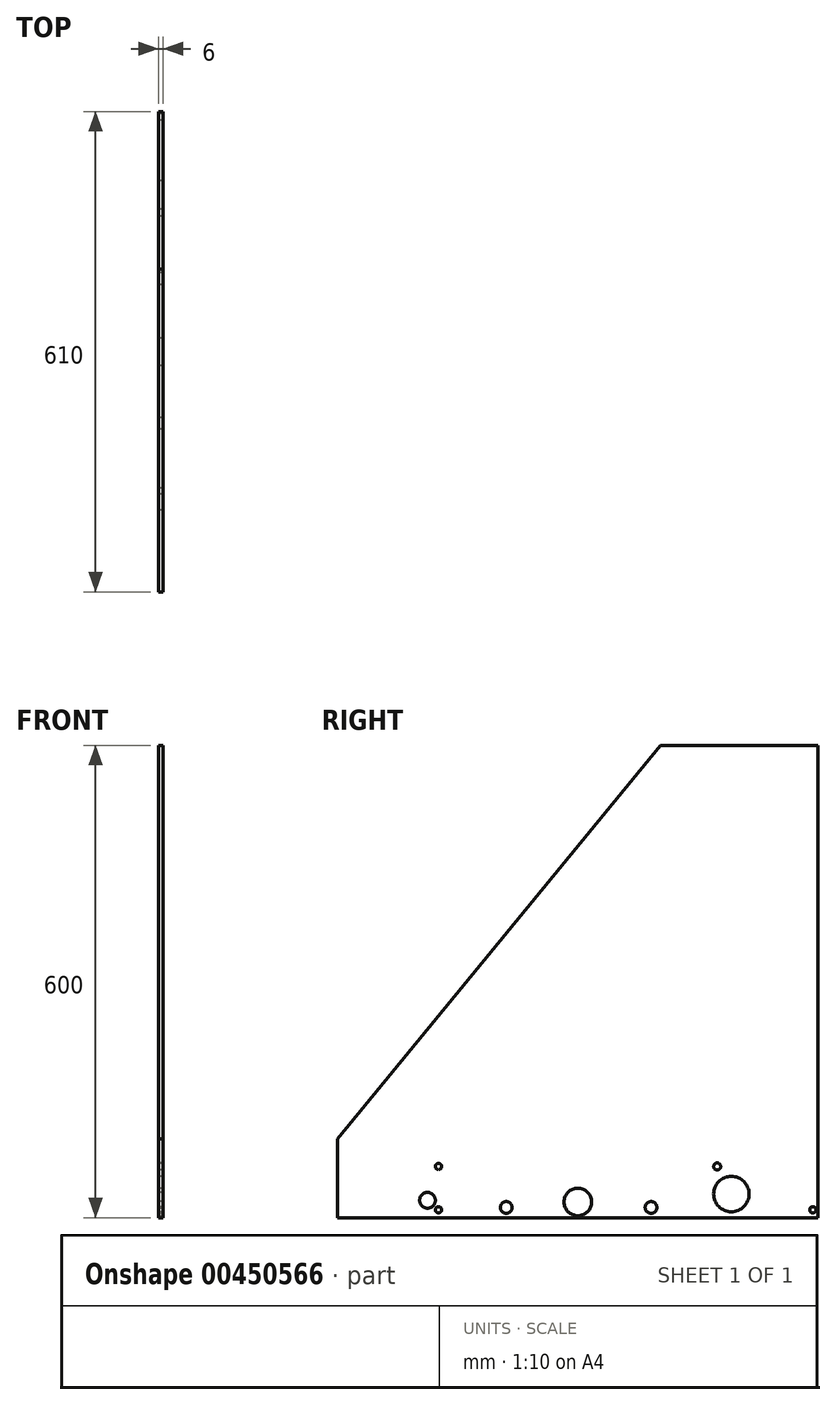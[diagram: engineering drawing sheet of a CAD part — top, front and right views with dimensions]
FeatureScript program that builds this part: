
annotation { "Feature Type Name" : "Feature", "Feature Type Description" : "" }
export const myFeature = defineFeature(function(context is Context, id is Id, definition is map)
    precondition{}
    {
        {
            var Q0;
            Q0=qCreatedBy(makeId("Right.planeOp"),FACE);
            var sketch = newSketch(context, id + "F0", { "sketchPlane" : qUnion([Q0])});
            skLineSegment(sketch, "E0", {"start": v(0, 0) * mm, "end": v(-610, 0) * mm});
            skLineSegment(sketch, "E1", {"start": v(-610, 0) * mm, "end": v(-610, 100) * mm});
            skLineSegment(sketch, "E2", {"start": v(0, 0) * mm, "end": v(0, 600) * mm});
            skLineSegment(sketch, "E3", {"start": v(0, 600) * mm, "end": v(-200, 600) * mm});
            skLineSegment(sketch, "E4", {"start": v(-610, 100) * mm, "end": v(-200, 600) * mm});
            skCircle(sketch, "E5", {"center": v(-6.5, 10) * mm, "radius": 4 * mm});
            skCircle(sketch, "E6", {"center": v(-110, 30) * mm, "radius": 22.5 * mm});
            skCircle(sketch, "E7", {"center": v(-128, 65) * mm, "radius": 4.5 * mm});
            skCircle(sketch, "E8", {"center": v(-212, 13) * mm, "radius": 7.5 * mm});
            skCircle(sketch, "E9", {"center": v(-305, 20) * mm, "radius": 17.5 * mm});
            skCircle(sketch, "E10", {"center": v(-396, 13) * mm, "radius": 7.5 * mm});
            skCircle(sketch, "E11", {"center": v(-482, 65) * mm, "radius": 4 * mm});
            skCircle(sketch, "E12", {"center": v(-482, 10) * mm, "radius": 4 * mm});
            skLineSegment(sketch, "E13", {"start": v(0, 0) * mm, "end": v(-496, 0) * mm});
            skCircle(sketch, "E14", {"center": v(-496, 22) * mm, "radius": 10 * mm});
            skSolve(sketch);
        }
        {
            var Q0;
            Q0=makeQuery(id+"F0.imprint","IMPRINT",FACE,{"disambiguationData":[TD([[makeQuery(id+"F0.imprint","IMPRINT",EDGE,{"derivedFrom":sQuery(id+"F0.wireOp",EDGE,"E0")}),-1.0]])]});
            extrude(context, id + "F1", {"entities" : qUnion([Q0]), "depth" : 6 * mm});
        }
    });
